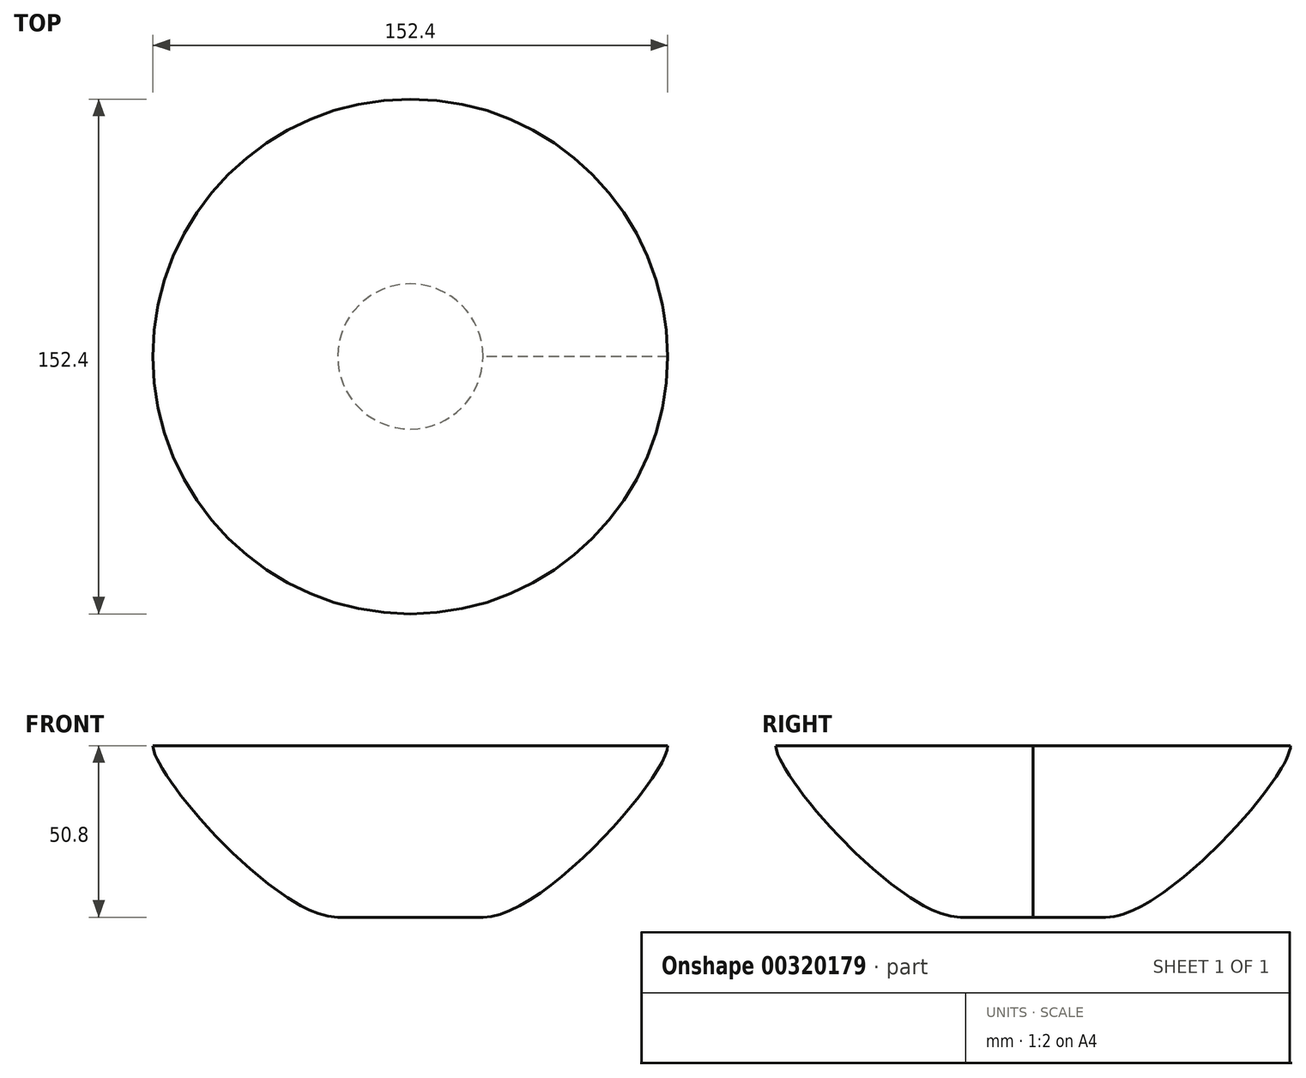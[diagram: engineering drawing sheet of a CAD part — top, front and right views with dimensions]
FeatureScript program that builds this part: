
annotation { "Feature Type Name" : "Feature", "Feature Type Description" : "" }
export const myFeature = defineFeature(function(context is Context, id is Id, definition is map)
    precondition{}
    {
        {
            var Q0;
            Q0=qCreatedBy(makeId("Top.planeOp"),FACE);
            var sketch = newSketch(context, id + "F0", { "sketchPlane" : qUnion([Q0])});
            skCircle(sketch, "E0", {"center": v(0, 0) * mm, "radius": 76.2 * mm});
            skSolve(sketch);
        }
        {
            var Q0;
            Q0=qCreatedBy(makeId("Top.planeOp"),FACE);
            cPlane(context, id + "F1", {"entities" : qUnion([Q0]), "cplaneType" : CPlaneType.OFFSET, "offset" : 50.8 * mm, "oppositeDirection" : true, "width" : 152.4 * mm, "height" : 152.4 * mm});
        }
        {
            var Q0;
            Q0=qCreatedBy(id+"F1.planeOp",FACE);
            var sketch = newSketch(context, id + "F2", { "sketchPlane" : qUnion([Q0])});
            skCircle(sketch, "E1", {"center": v(0, 0) * mm, "radius": 21.5 * mm});
            skSolve(sketch);
        }
        {
            var Q0;
            Q0=makeQuery(id+"F0.imprint","IMPRINT",FACE,{"disambiguationData":[TD([[makeQuery(id+"F0.imprint","IMPRINT",EDGE,{"derivedFrom":sQuery(id+"F0.wireOp",EDGE,"E0")}),1.0]])]});
            var Q1;
            Q1=makeQuery(id+"F2.imprint","IMPRINT",FACE,{"disambiguationData":[TD([[makeQuery(id+"F2.imprint","IMPRINT",EDGE,{"derivedFrom":sQuery(id+"F2.wireOp",EDGE,"E1")}),1.0]])]});
            loft(context, id + "F3", {"startCondition" : LoftEndDerivativeType.NORMAL_TO_PROFILE, "startMagnitude" : 1 / 2, "endCondition" : LoftEndDerivativeType.TANGENT_TO_PROFILE, "endMagnitude" : 1, "sheetProfilesArray" : [{ "sheetProfileEntities" : qUnion([Q0]) }, { "sheetProfileEntities" : qUnion([Q1]) }]});
        }
        {
            var Q0;
            Q0=qCreatedBy(makeId("Top.planeOp"),FACE);
            cPlane(context, id + "F4", {"entities" : qUnion([Q0]), "cplaneType" : CPlaneType.OFFSET, "offset" : 44.45 * mm, "oppositeDirection" : true, "width" : 152.4 * mm, "height" : 152.4 * mm});
        }
    });
